# Revit family: Protege5442F-Permanent
name_source: partatom
category: Specialty Equipment
units: mm (PartAtom-declared; Revit-internal decimal feet)

## family parameters
Always vertical = Yes
Classification Number = 23.50.05.14.17.11
Cut with Voids When Loaded = No
Enable Cutting in Views = No
Maintain Annotation Orientation = No
Part Type = Normal
Room Calculation Point = No
Round Connector Dimension = Use Diameter
Shared = No
Work Plane-Based = No

## types (1)
- Protege5442F-Permanent
    ACRYLIC WINDOW = Protege 5442 Acrylic window
    Assembly Code = D1010310
    Default Elevation = 0' - 0"
    Description = Vertical platform lift for persons with disabilities
    MEP Apparent Power = 1560 VA
    Manufacturer = Ascension, a division of AGM
    Model = Protege 5442P
    POWDER COATED SHEET METAL = Protege 5442 Powder Coat
    Structure = Protege 5442 Powder Coat
    URL = http://www.wheelchairlift.com
    Voltage_MEP = 120 V

## geometry (parser evidence)
native form markers: Sweep x3
no freeform markers — native parametric forms only
